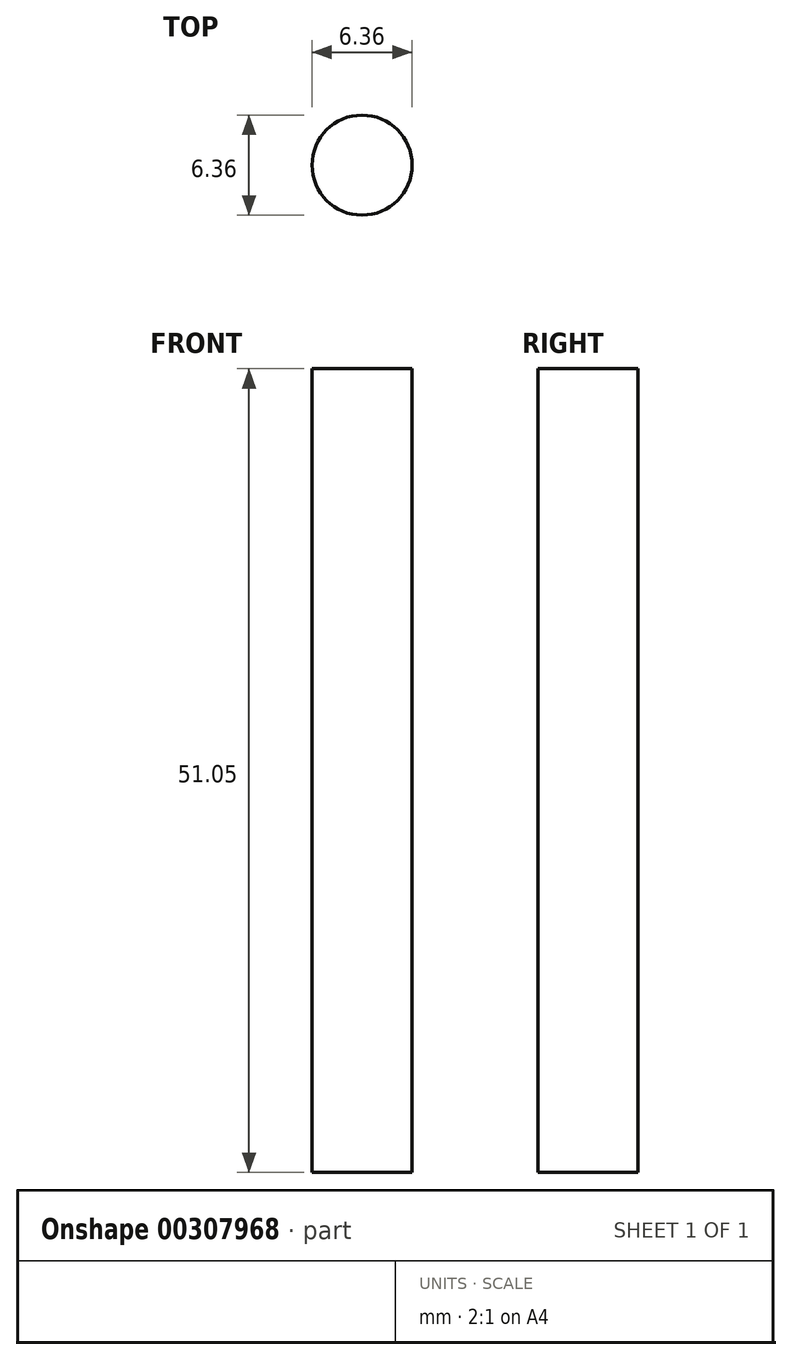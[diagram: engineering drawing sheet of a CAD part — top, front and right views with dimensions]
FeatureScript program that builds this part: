
annotation { "Feature Type Name" : "Feature", "Feature Type Description" : "" }
export const myFeature = defineFeature(function(context is Context, id is Id, definition is map)
    precondition{}
    {
        {
            var Q0;
            Q0=qCreatedBy(makeId("Top.planeOp"),FACE);
            var sketch = newSketch(context, id + "F0", { "sketchPlane" : qUnion([Q0])});
            skCircle(sketch, "E0", {"center": v(0, 0) * mm, "radius": 3.18 * mm});
            skSolve(sketch);
        }
        {
            var Q0;
            Q0 = qSketchRegion(id + "F0", true);
            extrude(context, id + "F1", {"entities" : qUnion([Q0]), "depth" : 51.05 * mm});
        }
    });
